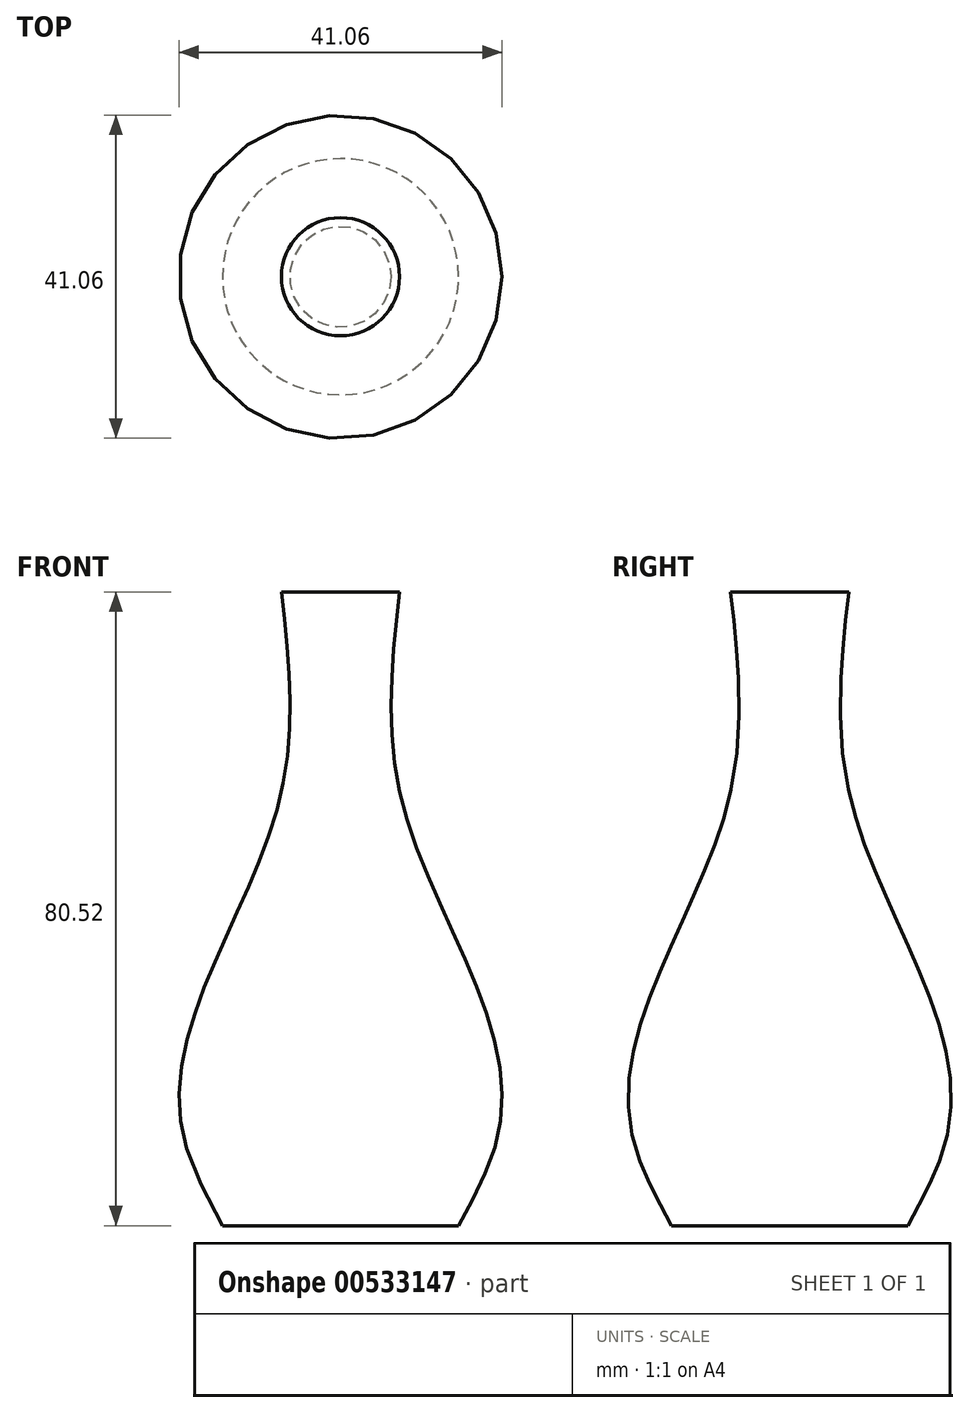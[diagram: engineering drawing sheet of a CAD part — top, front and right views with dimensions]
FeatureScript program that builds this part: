
annotation { "Feature Type Name" : "Feature", "Feature Type Description" : "" }
export const myFeature = defineFeature(function(context is Context, id is Id, definition is map)
    precondition{}
    {
        {
            var Q0;
            Q0=qCreatedBy(makeId("Top.planeOp"),FACE);
            var sketch = newSketch(context, id + "F0", { "sketchPlane" : qUnion([Q0])});
            skCircle(sketch, "E0", {"center": v(0, 0) * mm, "radius": 15 * mm});
            skSolve(sketch);
        }
        {
            var Q0;
            Q0=qCreatedBy(makeId("Top.planeOp"),FACE);
            cPlane(context, id + "F1", {"entities" : qUnion([Q0]), "cplaneType" : CPlaneType.OFFSET, "offset" : 11.43 * mm, "width" : 152.4 * mm, "height" : 152.4 * mm});
        }
        {
            var Q0;
            Q0=qCreatedBy(id+"F1.planeOp",FACE);
            var sketch = newSketch(context, id + "F2", { "sketchPlane" : qUnion([Q0])});
            skCircle(sketch, "E1", {"center": v(0, 0) * mm, "radius": 20 * mm});
            skSolve(sketch);
        }
        {
            var Q0;
            Q0=qCreatedBy(id+"F1.planeOp",FACE);
            cPlane(context, id + "F3", {"entities" : qUnion([Q0]), "cplaneType" : CPlaneType.OFFSET, "offset" : 43.69 * mm, "width" : 152.4 * mm, "height" : 152.4 * mm});
        }
        {
            var Q0;
            Q0=qCreatedBy(id+"F3.planeOp",FACE);
            var sketch = newSketch(context, id + "F4", { "sketchPlane" : qUnion([Q0])});
            skCircle(sketch, "E2", {"center": v(0, 0) * mm, "radius": 7.5 * mm});
            skSolve(sketch);
        }
        {
            var Q0;
            Q0=qCreatedBy(id+"F3.planeOp",FACE);
            cPlane(context, id + "F5", {"entities" : qUnion([Q0]), "cplaneType" : CPlaneType.OFFSET, "offset" : 25.4 * mm, "width" : 152.4 * mm, "height" : 152.4 * mm});
        }
        {
            var Q0;
            Q0=qCreatedBy(id+"F5.planeOp",FACE);
            var sketch = newSketch(context, id + "F6", { "sketchPlane" : qUnion([Q0])});
            skCircle(sketch, "E3", {"center": v(0, 0) * mm, "radius": 7.5 * mm});
            skSolve(sketch);
        }
        {
            var Q0;
            Q0 = qSketchRegion(id + "F0", true);
            var Q1;
            Q1 = qSketchRegion(id + "F2", true);
            var Q2;
            Q2 = qSketchRegion(id + "F4", true);
            var Q3;
            Q3 = qSketchRegion(id + "F6", true);
            loft(context, id + "F7", {"sheetProfilesArray" : [{ "sheetProfileEntities" : qUnion([Q0]) }, { "sheetProfileEntities" : qUnion([Q1]) }, { "sheetProfileEntities" : qUnion([Q2]) }, { "sheetProfileEntities" : qUnion([Q3]) }]});
        }
    });
